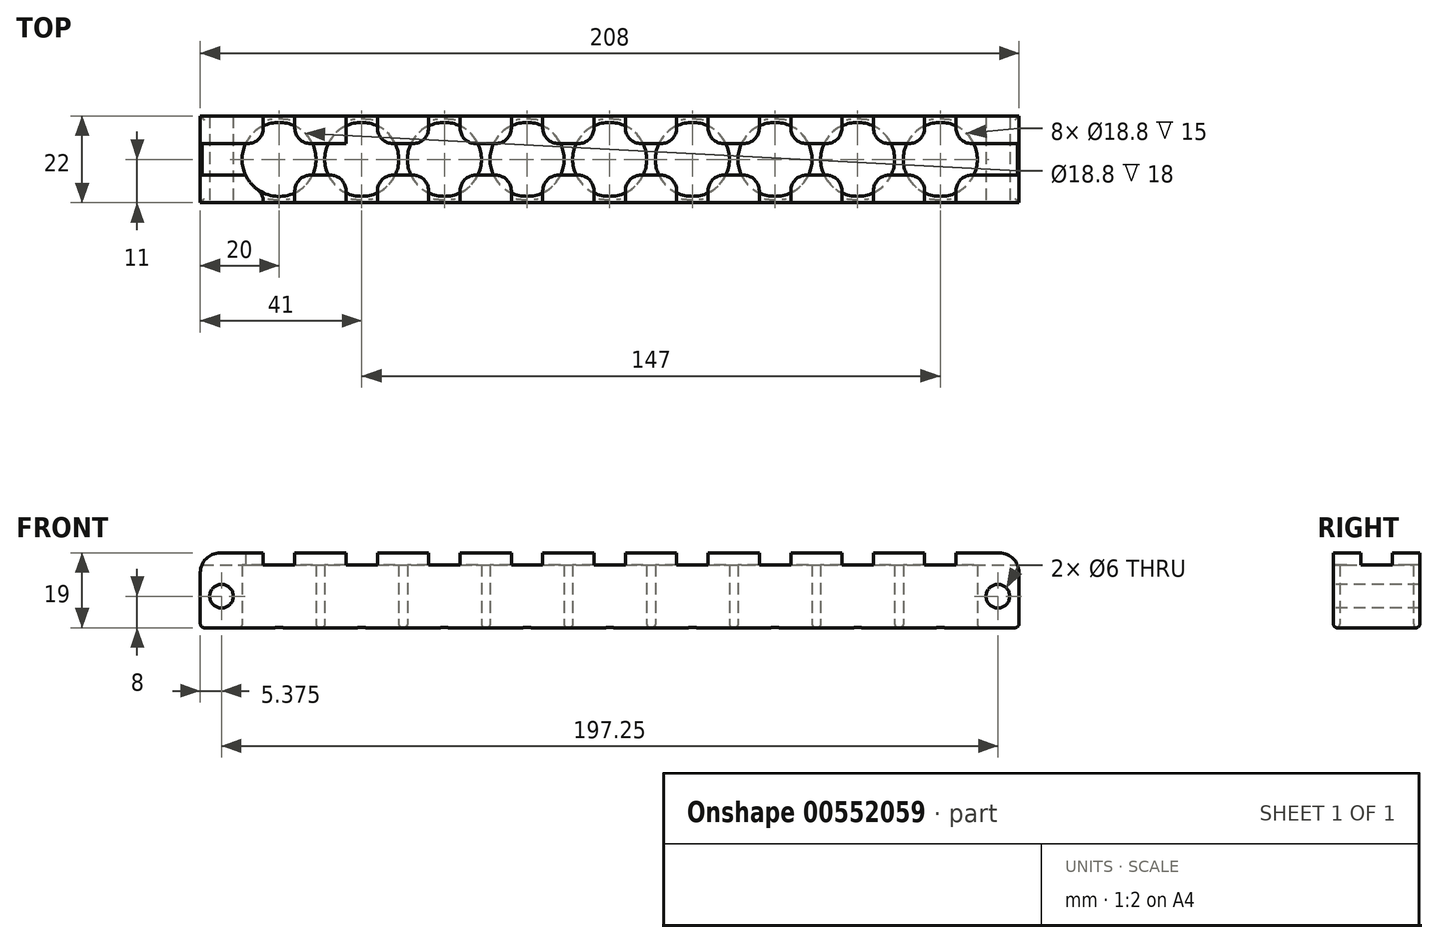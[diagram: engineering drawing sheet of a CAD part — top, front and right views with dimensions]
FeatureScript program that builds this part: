
annotation { "Feature Type Name" : "Feature", "Feature Type Description" : "" }
export const myFeature = defineFeature(function(context is Context, id is Id, definition is map)
    precondition{}
    {
        {
            var Q0;
            Q0=qCreatedBy(makeId("Top.planeOp"),FACE);
            var sketch = newSketch(context, id + "F0", { "sketchPlane" : qUnion([Q0])});
            skCircle(sketch, "E0", {"center": v(0, 0) * mm, "radius": 9.4 * mm});
            skCircle(sketch, "E1", {"center": v(-21, 0) * mm, "radius": 9.4 * mm});
            skCircle(sketch, "E2", {"center": v(-42, 0) * mm, "radius": 9.4 * mm});
            skCircle(sketch, "E3", {"center": v(-63, 0) * mm, "radius": 9.4 * mm});
            skCircle(sketch, "E4", {"center": v(84, 0) * mm, "radius": 9.4 * mm});
            skCircle(sketch, "E5", {"center": v(63, 0) * mm, "radius": 9.4 * mm});
            skCircle(sketch, "E6", {"center": v(42, 0) * mm, "radius": 9.4 * mm});
            skCircle(sketch, "E7", {"center": v(21, 0) * mm, "radius": 9.4 * mm});
            skCircle(sketch, "E8", {"center": v(105, 0) * mm, "radius": 9.4 * mm});
            skLineSegment(sketch, "E9.bottom", {"start": v(-83, 11) * mm, "end": v(125, 11) * mm});
            skLineSegment(sketch, "E9.top", {"start": v(-83, -11) * mm, "end": v(125, -11) * mm});
            skLineSegment(sketch, "E9.left", {"start": v(-83, 11) * mm, "end": v(-83, -11) * mm});
            skLineSegment(sketch, "E9.right", {"start": v(125, 11) * mm, "end": v(125, -11) * mm});
            skSolve(sketch);
        }
        {
            var Q0;
            Q0=makeQuery(id+"F0.imprint","IMPRINT",FACE,{"disambiguationData":[TD([[makeQuery(id+"F0.imprint","IMPRINT",EDGE,{"derivedFrom":sQuery(id+"F0.wireOp",EDGE,"E0")}),-1.0]])]});
            extrude(context, id + "F1", {"entities" : qUnion([Q0]), "depth" : 16 * mm, "offsetDistance" : 25 * mm});
        }
        {
            var Q0;
            Q0=makeQuery(id+"F1.opExtrude","SWEPT_FACE",FACE,{"disambiguationData":[OSD([sQuery(id+"F0.wireOp",EDGE,"E9.top")])]});
            var sketch = newSketch(context, id + "F2", { "sketchPlane" : qUnion([Q0])});
            skCircle(sketch, "E10", {"center": v(119.62, 8) * mm, "radius": 2.6 * mm});
            skPoint(sketch, "E10.centerSnap0", {"position": v(125, 8) * mm});
            skCircle(sketch, "E11", {"center": v(-77.62, 8) * mm, "radius": 2.6 * mm});
            skPoint(sketch, "E12", {"position": v(-83, 8) * mm});
            skSolve(sketch);
        }
        {
            var Q0;
            Q0=makeQuery(id+"F1.opExtrude","CAP_FACE",FACE,{"disambiguationData":[OSD([sQuery(id+"F0.wireOp",EDGE,"E0"),sQuery(id+"F0.wireOp",EDGE,"E1"),sQuery(id+"F0.wireOp",EDGE,"E2"),sQuery(id+"F0.wireOp",EDGE,"E3"),sQuery(id+"F0.wireOp",EDGE,"E4"),sQuery(id+"F0.wireOp",EDGE,"E5"),sQuery(id+"F0.wireOp",EDGE,"E6"),sQuery(id+"F0.wireOp",EDGE,"E7"),sQuery(id+"F0.wireOp",EDGE,"E8"),sQuery(id+"F0.wireOp",EDGE,"E9.bottom"),sQuery(id+"F0.wireOp",EDGE,"E9.top"),sQuery(id+"F0.wireOp",EDGE,"E9.left"),sQuery(id+"F0.wireOp",EDGE,"E9.right")])],"isStart":false});
            var sketch = newSketch(context, id + "F3", { "sketchPlane" : qUnion([Q0])});
            skLineSegment(sketch, "E13", {"start": v(-83, -4) * mm, "end": v(-67, -4) * mm});
            skLineSegment(sketch, "E14", {"start": v(-83, 4) * mm, "end": v(-67, 4) * mm});
            skLineSegment(sketch, "E15", {"start": v(4, 11) * mm, "end": v(4, 4) * mm});
            skLineSegment(sketch, "E16", {"start": v(-4, 11) * mm, "end": v(-4, 4) * mm});
            skLineSegment(sketch, "E17", {"start": v(-59, 11) * mm, "end": v(-59, 4) * mm});
            skLineSegment(sketch, "E18", {"start": v(-67, 11) * mm, "end": v(-67, 4) * mm});
            skLineSegment(sketch, "E19", {"start": v(-38, 11) * mm, "end": v(-38, 4) * mm});
            skLineSegment(sketch, "E20", {"start": v(-46, 11) * mm, "end": v(-46, 4) * mm});
            skLineSegment(sketch, "E21", {"start": v(-46, -11) * mm, "end": v(-38, -11) * mm});
            skLineSegment(sketch, "E22", {"start": v(-25, 11) * mm, "end": v(-25, 4) * mm});
            skLineSegment(sketch, "E23", {"start": v(17, 11) * mm, "end": v(17, 4) * mm});
            skLineSegment(sketch, "E24", {"start": v(17, -11) * mm, "end": v(25, -11) * mm});
            skLineSegment(sketch, "E25", {"start": v(46, 11) * mm, "end": v(46, 4) * mm});
            skLineSegment(sketch, "E26", {"start": v(38, 11) * mm, "end": v(38, 4) * mm});
            skLineSegment(sketch, "E27", {"start": v(38, -11) * mm, "end": v(46, -11) * mm});
            skLineSegment(sketch, "E28", {"start": v(67, 11) * mm, "end": v(67, 4) * mm});
            skLineSegment(sketch, "E29", {"start": v(59, -11) * mm, "end": v(67, -11) * mm});
            skLineSegment(sketch, "E30", {"start": v(88, 11) * mm, "end": v(88, 4) * mm});
            skLineSegment(sketch, "E31", {"start": v(80, 11) * mm, "end": v(80, 4) * mm});
            skLineSegment(sketch, "E32", {"start": v(109, 11) * mm, "end": v(109, 4) * mm});
            skLineSegment(sketch, "E33", {"start": v(101, 11) * mm, "end": v(101, 4) * mm});
            skLineSegment(sketch, "E34", {"start": v(-83, -4) * mm, "end": v(-83, -11) * mm});
            skLineSegment(sketch, "E35", {"start": v(-83, -11) * mm, "end": v(-67, -11) * mm});
            skLineSegment(sketch, "E36", {"start": v(-67, -4) * mm, "end": v(-83, -4) * mm});
            skPoint(sketch, "E37", {"position": v(-67, 4) * mm});
            skPoint(sketch, "E38", {"position": v(-59, 4) * mm});
            skPoint(sketch, "E39", {"position": v(-59, -4) * mm});
            skPoint(sketch, "E40", {"position": v(-46, 4) * mm});
            skPoint(sketch, "E41", {"position": v(-46, -4) * mm});
            skLineSegment(sketch, "E42.trimOffspring", {"start": v(-67, -4) * mm, "end": v(-67, -11) * mm});
            skLineSegment(sketch, "E43.trimOffspring", {"start": v(-59, -4) * mm, "end": v(-46, -4) * mm});
            skLineSegment(sketch, "E44.trimOffspring", {"start": v(-59, -4) * mm, "end": v(-59, -11) * mm});
            skLineSegment(sketch, "E45.trimOffspring", {"start": v(-59, 4) * mm, "end": v(-46, 4) * mm});
            skLineSegment(sketch, "E46.trimOffspring", {"start": v(-46, -4) * mm, "end": v(-46, -11) * mm});
            skLineSegment(sketch, "E47.trimOffspring", {"start": v(-38, 4) * mm, "end": v(-25, 4) * mm});
            skLineSegment(sketch, "E48.trimOffspring", {"start": v(-38, -4) * mm, "end": v(-38, -11) * mm});
            skLineSegment(sketch, "E49.trimOffspring", {"start": v(-25, -4) * mm, "end": v(-25, -11) * mm});
            skLineSegment(sketch, "E50.trimOffspring", {"start": v(-17, 4) * mm, "end": v(-4, 4) * mm});
            skLineSegment(sketch, "E51.trimOffspring", {"start": v(-17, -4) * mm, "end": v(-17, -11) * mm});
            skLineSegment(sketch, "E52", {"start": v(-17, 4) * mm, "end": v(-17, 11) * mm});
            skLineSegment(sketch, "E53.trimOffspring", {"start": v(-4, -4) * mm, "end": v(-4, -11) * mm});
            skLineSegment(sketch, "E54.trimOffspring", {"start": v(4, -4) * mm, "end": v(4, -11) * mm});
            skLineSegment(sketch, "E55.trimOffspring", {"start": v(4, -4) * mm, "end": v(17, -4) * mm});
            skLineSegment(sketch, "E56.trimOffspring", {"start": v(17, -4) * mm, "end": v(17, -11) * mm});
            skLineSegment(sketch, "E57.trimOffspring", {"start": v(25, 4) * mm, "end": v(38, 4) * mm});
            skLineSegment(sketch, "E58.trimOffspring", {"start": v(25, -4) * mm, "end": v(25, -11) * mm});
            skLineSegment(sketch, "E59.trimOffspring", {"start": v(38, -4) * mm, "end": v(38, -11) * mm});
            skLineSegment(sketch, "E60.trimOffspring", {"start": v(46, 4) * mm, "end": v(59, 4) * mm});
            skLineSegment(sketch, "E61.trimOffspring", {"start": v(46, -4) * mm, "end": v(46, -11) * mm});
            skLineSegment(sketch, "E62.trimOffspring", {"start": v(-38, -4) * mm, "end": v(-25, -4) * mm});
            skLineSegment(sketch, "E63.trimOffspring", {"start": v(4, 4) * mm, "end": v(17, 4) * mm});
            skLineSegment(sketch, "E64.trimOffspring", {"start": v(-17, -4) * mm, "end": v(-4, -4) * mm});
            skLineSegment(sketch, "E65.trimOffspring", {"start": v(25, -4) * mm, "end": v(38, -4) * mm});
            skLineSegment(sketch, "E66.trimOffspring", {"start": v(46, -4) * mm, "end": v(59, -4) * mm});
            skLineSegment(sketch, "E67.trimOffspring", {"start": v(67, -4) * mm, "end": v(80, -4) * mm});
            skPoint(sketch, "E68.orphan", {"position": v(25, 11) * mm});
            skLineSegment(sketch, "E69.trimOffspring", {"start": v(67, 4) * mm, "end": v(80, 4) * mm});
            skLineSegment(sketch, "E70.trimOffspring", {"start": v(59, -4) * mm, "end": v(59, -11) * mm});
            skPoint(sketch, "E71.start.orphan", {"position": v(59, 11) * mm});
            skLineSegment(sketch, "E72.trimOffspring", {"start": v(67, -4) * mm, "end": v(67, -11) * mm});
            skLineSegment(sketch, "E73.trimOffspring", {"start": v(80, -4) * mm, "end": v(80, -11) * mm});
            skLineSegment(sketch, "E74.trimOffspring", {"start": v(88, -4) * mm, "end": v(88, -11) * mm});
            skLineSegment(sketch, "E75.trimOffspring", {"start": v(88, 4) * mm, "end": v(101, 4) * mm});
            skPoint(sketch, "E76.orphan", {"position": v(105, 11) * mm});
            skLineSegment(sketch, "E77.trimOffspring", {"start": v(109, 4) * mm, "end": v(125, 4) * mm});
            skLineSegment(sketch, "E78.trimOffspring", {"start": v(109, -4) * mm, "end": v(109, -11) * mm});
            skLineSegment(sketch, "E79.trimOffspring", {"start": v(109, -4) * mm, "end": v(125, -4) * mm});
            skLineSegment(sketch, "E80.trimOffspring", {"start": v(101, -4) * mm, "end": v(101, -11) * mm});
            skLineSegment(sketch, "E81.trimOffspring", {"start": v(88, -4) * mm, "end": v(101, -4) * mm});
            skLineSegment(sketch, "E82", {"start": v(59, 4) * mm, "end": v(59, 11) * mm});
            skLineSegment(sketch, "E83", {"start": v(25, 4) * mm, "end": v(25, 11) * mm});
            skLineSegment(sketch, "E84", {"start": v(-83, 4) * mm, "end": v(-83, 11) * mm});
            skLineSegment(sketch, "E85", {"start": v(-83, 11) * mm, "end": v(-67, 11) * mm});
            skSolve(sketch);
        }
        {
            var Q0;
            {var subQ0=sQuery(id+"F3.wireOp",EDGE,"E84");Q0=makeQuery(id+"F3.imprint","IMPRINT",FACE,{"disambiguationData":[TD([[makeQuery(id+"F3.imprint","IMPRINT",EDGE,{"derivedFrom":subQ0}),1.0]])]});}
            var Q1;
            {var subQ0=sQuery(id+"F3.wireOp",EDGE,"E18");var subQ1=sQuery(id+"F3.wireOp",EDGE,"E14");var subQ2=makeQuery(id+"F3.imprint","INTERSECT",VERTEX,{"derivedFrom":[subQ1,subQ0]});Q1=makeQuery(id+"F3.imprint","IMPRINT",FACE,{"disambiguationData":[TD([[makeQuery(id+"F3.imprint","IMPRINT",EDGE,{"disambiguationData":[TD([[subQ2,1.0]])],"derivedFrom":subQ1}),1.0]])]});}
            var Q2;
            {var subQ1=sQuery(id+"F3.wireOp",EDGE,"E34");Q2=makeQuery(id+"F3.imprint","IMPRINT",FACE,{"disambiguationData":[TD([[makeQuery(id+"F3.imprint","IMPRINT",EDGE,{"derivedFrom":subQ1}),1.0]])]});}
            var Q3;
            {var subQ0=sQuery(id+"F3.wireOp",EDGE,"E42.trimOffspring");var subQ1=sQuery(id+"F3.wireOp",EDGE,"E36");var subQ2=makeQuery(id+"F3.imprint","INTERSECT",VERTEX,{"derivedFrom":[subQ1,subQ0]});Q3=makeQuery(id+"F3.imprint","IMPRINT",FACE,{"disambiguationData":[TD([[makeQuery(id+"F3.imprint","IMPRINT",EDGE,{"disambiguationData":[TD([[subQ2,-1.0]])],"derivedFrom":subQ1}),1.0]])]});}
            var Q4;
            {var subQ0=sQuery(id+"F3.wireOp",EDGE,"E45.trimOffspring");var subQ1=sQuery(id+"F3.wireOp",EDGE,"E17");var subQ2=makeQuery(id+"F3.imprint","INTERSECT",VERTEX,{"derivedFrom":[subQ1,subQ0]});Q4=makeQuery(id+"F3.imprint","IMPRINT",FACE,{"disambiguationData":[TD([[makeQuery(id+"F3.imprint","IMPRINT",EDGE,{"disambiguationData":[TD([[subQ2,1.0]])],"derivedFrom":subQ1}),1.0]])]});}
            var Q5;
            {var subQ5=sQuery(id+"F3.wireOp",EDGE,"E17");var subQ6=makeQuery(id+"F1.opExtrude","CAP_EDGE",EDGE,{"disambiguationData":[OSD([sQuery(id+"F0.wireOp",EDGE,"E9.bottom")])],"isStart":false});var subQ7=makeQuery(id+"F3.imprint","INTERSECT",VERTEX,{"derivedFrom":[subQ6,subQ5]});Q5=makeQuery(id+"F3.imprint","IMPRINT",FACE,{"disambiguationData":[TD([[makeQuery(id+"F3.imprint","IMPRINT",EDGE,{"disambiguationData":[TD([[subQ7,-1.0]])],"derivedFrom":subQ5}),1.0]])]});}
            var Q6;
            {var subQ0=sQuery(id+"F3.wireOp",EDGE,"E45.trimOffspring");var subQ1=sQuery(id+"F3.wireOp",EDGE,"E20");var subQ2=makeQuery(id+"F3.imprint","INTERSECT",VERTEX,{"derivedFrom":[subQ1,subQ0]});Q6=makeQuery(id+"F3.imprint","IMPRINT",FACE,{"disambiguationData":[TD([[makeQuery(id+"F3.imprint","IMPRINT",EDGE,{"disambiguationData":[TD([[subQ2,1.0]])],"derivedFrom":subQ1}),-1.0]])]});}
            var Q7;
            {var subQ0=sQuery(id+"F3.wireOp",EDGE,"E44.trimOffspring");var subQ1=sQuery(id+"F3.wireOp",EDGE,"E43.trimOffspring");var subQ2=makeQuery(id+"F3.imprint","INTERSECT",VERTEX,{"derivedFrom":[subQ1,subQ0]});Q7=makeQuery(id+"F3.imprint","IMPRINT",FACE,{"disambiguationData":[TD([[makeQuery(id+"F3.imprint","IMPRINT",EDGE,{"disambiguationData":[TD([[subQ2,-1.0]])],"derivedFrom":subQ1}),-1.0]])]});}
            var Q8;
            {var subQ0=sQuery(id+"F3.wireOp",EDGE,"E46.trimOffspring");var subQ1=sQuery(id+"F3.wireOp",EDGE,"E43.trimOffspring");var subQ2=makeQuery(id+"F3.imprint","INTERSECT",VERTEX,{"derivedFrom":[subQ1,subQ0]});Q8=makeQuery(id+"F3.imprint","IMPRINT",FACE,{"disambiguationData":[TD([[makeQuery(id+"F3.imprint","IMPRINT",EDGE,{"disambiguationData":[TD([[subQ2,1.0]])],"derivedFrom":subQ1}),-1.0]])]});}
            var Q9;
            {var subQ5=makeQuery(id+"F1.opExtrude","CAP_EDGE",EDGE,{"disambiguationData":[OSD([sQuery(id+"F0.wireOp",EDGE,"E3")])],"isStart":false});var subQ9=sQuery(id+"F3.wireOp",EDGE,"E43.trimOffspring");var subQ10=makeQuery(id+"F3.imprint","INTERSECT",VERTEX,{"derivedFrom":[subQ5,subQ9]});Q9=makeQuery(id+"F3.imprint","IMPRINT",FACE,{"disambiguationData":[TD([[makeQuery(id+"F3.imprint","IMPRINT",EDGE,{"disambiguationData":[TD([[subQ10,-1.0]])],"derivedFrom":subQ9}),-1.0]])]});}
            var Q10;
            {var subQ1=makeQuery(id+"F1.opExtrude","CAP_EDGE",EDGE,{"disambiguationData":[OSD([sQuery(id+"F0.wireOp",EDGE,"E9.top")])],"isStart":false});var subQ3=sQuery(id+"F3.wireOp",EDGE,"E49.trimOffspring");var subQ4=makeQuery(id+"F3.imprint","INTERSECT",VERTEX,{"derivedFrom":[subQ1,subQ3]});Q10=makeQuery(id+"F3.imprint","IMPRINT",FACE,{"disambiguationData":[TD([[makeQuery(id+"F3.imprint","IMPRINT",EDGE,{"disambiguationData":[TD([[subQ4,1.0]])],"derivedFrom":subQ3}),-1.0]])]});}
            var Q11;
            {var subQ0=sQuery(id+"F3.wireOp",EDGE,"E62.trimOffspring");var subQ1=sQuery(id+"F3.wireOp",EDGE,"E48.trimOffspring");var subQ2=makeQuery(id+"F3.imprint","INTERSECT",VERTEX,{"derivedFrom":[subQ1,subQ0]});Q11=makeQuery(id+"F3.imprint","IMPRINT",FACE,{"disambiguationData":[TD([[makeQuery(id+"F3.imprint","IMPRINT",EDGE,{"disambiguationData":[TD([[subQ2,-1.0]])],"derivedFrom":subQ1}),1.0]])]});}
            var Q12;
            {var subQ0=sQuery(id+"F3.wireOp",EDGE,"E62.trimOffspring");var subQ1=sQuery(id+"F3.wireOp",EDGE,"E49.trimOffspring");var subQ2=makeQuery(id+"F3.imprint","INTERSECT",VERTEX,{"derivedFrom":[subQ1,subQ0]});Q12=makeQuery(id+"F3.imprint","IMPRINT",FACE,{"disambiguationData":[TD([[makeQuery(id+"F3.imprint","IMPRINT",EDGE,{"disambiguationData":[TD([[subQ2,-1.0]])],"derivedFrom":subQ1}),-1.0]])]});}
            var Q13;
            {var subQ0=sQuery(id+"F3.wireOp",EDGE,"E19");var subQ1=makeQuery(id+"F1.opExtrude","CAP_EDGE",EDGE,{"disambiguationData":[OSD([sQuery(id+"F0.wireOp",EDGE,"E9.bottom")])],"isStart":false});var subQ2=makeQuery(id+"F3.imprint","INTERSECT",VERTEX,{"derivedFrom":[subQ1,subQ0]});Q13=makeQuery(id+"F3.imprint","IMPRINT",FACE,{"disambiguationData":[TD([[makeQuery(id+"F3.imprint","IMPRINT",EDGE,{"disambiguationData":[TD([[subQ2,-1.0]])],"derivedFrom":subQ0}),1.0]])]});}
            var Q14;
            {var subQ0=sQuery(id+"F3.wireOp",EDGE,"E47.trimOffspring");var subQ1=sQuery(id+"F3.wireOp",EDGE,"E22");var subQ2=makeQuery(id+"F3.imprint","INTERSECT",VERTEX,{"derivedFrom":[subQ1,subQ0]});Q14=makeQuery(id+"F3.imprint","IMPRINT",FACE,{"disambiguationData":[TD([[makeQuery(id+"F3.imprint","IMPRINT",EDGE,{"disambiguationData":[TD([[subQ2,1.0]])],"derivedFrom":subQ1}),-1.0]])]});}
            var Q15;
            {var subQ0=sQuery(id+"F3.wireOp",EDGE,"E47.trimOffspring");var subQ1=sQuery(id+"F3.wireOp",EDGE,"E19");var subQ2=makeQuery(id+"F3.imprint","INTERSECT",VERTEX,{"derivedFrom":[subQ1,subQ0]});Q15=makeQuery(id+"F3.imprint","IMPRINT",FACE,{"disambiguationData":[TD([[makeQuery(id+"F3.imprint","IMPRINT",EDGE,{"disambiguationData":[TD([[subQ2,1.0]])],"derivedFrom":subQ1}),1.0]])]});}
            var Q16;
            {var subQ0=sQuery(id+"F3.wireOp",EDGE,"E52");var subQ1=sQuery(id+"F3.wireOp",EDGE,"E50.trimOffspring");var subQ2=makeQuery(id+"F3.imprint","INTERSECT",VERTEX,{"derivedFrom":[subQ1,subQ0]});Q16=makeQuery(id+"F3.imprint","IMPRINT",FACE,{"disambiguationData":[TD([[makeQuery(id+"F3.imprint","IMPRINT",EDGE,{"disambiguationData":[TD([[subQ2,-1.0]])],"derivedFrom":subQ1}),1.0]])]});}
            var Q17;
            {var subQ0=sQuery(id+"F3.wireOp",EDGE,"E16");var subQ1=makeQuery(id+"F1.opExtrude","CAP_EDGE",EDGE,{"disambiguationData":[OSD([sQuery(id+"F0.wireOp",EDGE,"E9.bottom")])],"isStart":false});var subQ2=makeQuery(id+"F3.imprint","INTERSECT",VERTEX,{"derivedFrom":[subQ1,subQ0]});Q17=makeQuery(id+"F3.imprint","IMPRINT",FACE,{"disambiguationData":[TD([[makeQuery(id+"F3.imprint","IMPRINT",EDGE,{"disambiguationData":[TD([[subQ2,-1.0]])],"derivedFrom":subQ0}),-1.0]])]});}
            var Q18;
            {var subQ0=sQuery(id+"F3.wireOp",EDGE,"E50.trimOffspring");var subQ1=sQuery(id+"F3.wireOp",EDGE,"E16");var subQ2=makeQuery(id+"F3.imprint","INTERSECT",VERTEX,{"derivedFrom":[subQ1,subQ0]});Q18=makeQuery(id+"F3.imprint","IMPRINT",FACE,{"disambiguationData":[TD([[makeQuery(id+"F3.imprint","IMPRINT",EDGE,{"disambiguationData":[TD([[subQ2,1.0]])],"derivedFrom":subQ1}),-1.0]])]});}
            var Q19;
            {var subQ0=sQuery(id+"F3.wireOp",EDGE,"E51.trimOffspring");var subQ1=makeQuery(id+"F1.opExtrude","CAP_EDGE",EDGE,{"disambiguationData":[OSD([sQuery(id+"F0.wireOp",EDGE,"E9.top")])],"isStart":false});var subQ2=makeQuery(id+"F3.imprint","INTERSECT",VERTEX,{"derivedFrom":[subQ1,subQ0]});Q19=makeQuery(id+"F3.imprint","IMPRINT",FACE,{"disambiguationData":[TD([[makeQuery(id+"F3.imprint","IMPRINT",EDGE,{"disambiguationData":[TD([[subQ2,1.0]])],"derivedFrom":subQ0}),1.0]])]});}
            var Q20;
            {var subQ0=sQuery(id+"F3.wireOp",EDGE,"E64.trimOffspring");var subQ1=sQuery(id+"F3.wireOp",EDGE,"E51.trimOffspring");var subQ2=makeQuery(id+"F3.imprint","INTERSECT",VERTEX,{"derivedFrom":[subQ1,subQ0]});Q20=makeQuery(id+"F3.imprint","IMPRINT",FACE,{"disambiguationData":[TD([[makeQuery(id+"F3.imprint","IMPRINT",EDGE,{"disambiguationData":[TD([[subQ2,-1.0]])],"derivedFrom":subQ1}),1.0]])]});}
            var Q21;
            {var subQ0=sQuery(id+"F3.wireOp",EDGE,"E64.trimOffspring");var subQ1=sQuery(id+"F3.wireOp",EDGE,"E53.trimOffspring");var subQ2=makeQuery(id+"F3.imprint","INTERSECT",VERTEX,{"derivedFrom":[subQ1,subQ0]});Q21=makeQuery(id+"F3.imprint","IMPRINT",FACE,{"disambiguationData":[TD([[makeQuery(id+"F3.imprint","IMPRINT",EDGE,{"disambiguationData":[TD([[subQ2,-1.0]])],"derivedFrom":subQ1}),-1.0]])]});}
            var Q22;
            {var subQ0=sQuery(id+"F3.wireOp",EDGE,"E63.trimOffspring");var subQ1=sQuery(id+"F3.wireOp",EDGE,"E15");var subQ2=makeQuery(id+"F3.imprint","INTERSECT",VERTEX,{"derivedFrom":[subQ1,subQ0]});Q22=makeQuery(id+"F3.imprint","IMPRINT",FACE,{"disambiguationData":[TD([[makeQuery(id+"F3.imprint","IMPRINT",EDGE,{"disambiguationData":[TD([[subQ2,1.0]])],"derivedFrom":subQ1}),1.0]])]});}
            var Q23;
            {var subQ0=sQuery(id+"F3.wireOp",EDGE,"E15");var subQ1=makeQuery(id+"F1.opExtrude","CAP_EDGE",EDGE,{"disambiguationData":[OSD([sQuery(id+"F0.wireOp",EDGE,"E9.bottom")])],"isStart":false});var subQ2=makeQuery(id+"F3.imprint","INTERSECT",VERTEX,{"derivedFrom":[subQ1,subQ0]});Q23=makeQuery(id+"F3.imprint","IMPRINT",FACE,{"disambiguationData":[TD([[makeQuery(id+"F3.imprint","IMPRINT",EDGE,{"disambiguationData":[TD([[subQ2,-1.0]])],"derivedFrom":subQ0}),1.0]])]});}
            var Q24;
            {var subQ0=sQuery(id+"F3.wireOp",EDGE,"E63.trimOffspring");var subQ1=sQuery(id+"F3.wireOp",EDGE,"E23");var subQ2=makeQuery(id+"F3.imprint","INTERSECT",VERTEX,{"derivedFrom":[subQ1,subQ0]});Q24=makeQuery(id+"F3.imprint","IMPRINT",FACE,{"disambiguationData":[TD([[makeQuery(id+"F3.imprint","IMPRINT",EDGE,{"disambiguationData":[TD([[subQ2,1.0]])],"derivedFrom":subQ1}),-1.0]])]});}
            var Q25;
            {var subQ0=sQuery(id+"F3.wireOp",EDGE,"E55.trimOffspring");var subQ1=sQuery(id+"F3.wireOp",EDGE,"E54.trimOffspring");var subQ2=makeQuery(id+"F3.imprint","INTERSECT",VERTEX,{"derivedFrom":[subQ1,subQ0]});Q25=makeQuery(id+"F3.imprint","IMPRINT",FACE,{"disambiguationData":[TD([[makeQuery(id+"F3.imprint","IMPRINT",EDGE,{"disambiguationData":[TD([[subQ2,-1.0]])],"derivedFrom":subQ1}),1.0]])]});}
            var Q26;
            {var subQ1=makeQuery(id+"F1.opExtrude","CAP_EDGE",EDGE,{"disambiguationData":[OSD([sQuery(id+"F0.wireOp",EDGE,"E9.top")])],"isStart":false});var subQ3=sQuery(id+"F3.wireOp",EDGE,"E54.trimOffspring");var subQ4=makeQuery(id+"F3.imprint","INTERSECT",VERTEX,{"derivedFrom":[subQ1,subQ3]});Q26=makeQuery(id+"F3.imprint","IMPRINT",FACE,{"disambiguationData":[TD([[makeQuery(id+"F3.imprint","IMPRINT",EDGE,{"disambiguationData":[TD([[subQ4,1.0]])],"derivedFrom":subQ3}),1.0]])]});}
            var Q27;
            {var subQ0=sQuery(id+"F3.wireOp",EDGE,"E56.trimOffspring");var subQ1=sQuery(id+"F3.wireOp",EDGE,"E55.trimOffspring");var subQ2=makeQuery(id+"F3.imprint","INTERSECT",VERTEX,{"derivedFrom":[subQ1,subQ0]});Q27=makeQuery(id+"F3.imprint","IMPRINT",FACE,{"disambiguationData":[TD([[makeQuery(id+"F3.imprint","IMPRINT",EDGE,{"disambiguationData":[TD([[subQ2,1.0]])],"derivedFrom":subQ1}),-1.0]])]});}
            var Q28;
            {var subQ0=sQuery(id+"F3.wireOp",EDGE,"E65.trimOffspring");var subQ1=sQuery(id+"F3.wireOp",EDGE,"E58.trimOffspring");var subQ2=makeQuery(id+"F3.imprint","INTERSECT",VERTEX,{"derivedFrom":[subQ1,subQ0]});Q28=makeQuery(id+"F3.imprint","IMPRINT",FACE,{"disambiguationData":[TD([[makeQuery(id+"F3.imprint","IMPRINT",EDGE,{"disambiguationData":[TD([[subQ2,-1.0]])],"derivedFrom":subQ1}),1.0]])]});}
            var Q29;
            {var subQ0=sQuery(id+"F3.wireOp",EDGE,"E65.trimOffspring");var subQ1=makeQuery(id+"F1.opExtrude","CAP_EDGE",EDGE,{"disambiguationData":[OSD([sQuery(id+"F0.wireOp",EDGE,"E7")])],"isStart":false});var subQ2=makeQuery(id+"F3.imprint","INTERSECT",VERTEX,{"derivedFrom":[subQ1,subQ0]});Q29=makeQuery(id+"F3.imprint","IMPRINT",FACE,{"disambiguationData":[TD([[makeQuery(id+"F3.imprint","IMPRINT",EDGE,{"disambiguationData":[TD([[subQ2,-1.0]])],"derivedFrom":subQ0}),-1.0]])]});}
            var Q30;
            {var subQ0=sQuery(id+"F3.wireOp",EDGE,"E65.trimOffspring");var subQ1=sQuery(id+"F3.wireOp",EDGE,"E59.trimOffspring");var subQ2=makeQuery(id+"F3.imprint","INTERSECT",VERTEX,{"derivedFrom":[subQ1,subQ0]});Q30=makeQuery(id+"F3.imprint","IMPRINT",FACE,{"disambiguationData":[TD([[makeQuery(id+"F3.imprint","IMPRINT",EDGE,{"disambiguationData":[TD([[subQ2,-1.0]])],"derivedFrom":subQ1}),-1.0]])]});}
            var Q31;
            {var subQ0=sQuery(id+"F3.wireOp",EDGE,"E83");var subQ1=sQuery(id+"F3.wireOp",EDGE,"E57.trimOffspring");var subQ2=makeQuery(id+"F3.imprint","INTERSECT",VERTEX,{"derivedFrom":[subQ1,subQ0]});Q31=makeQuery(id+"F3.imprint","IMPRINT",FACE,{"disambiguationData":[TD([[makeQuery(id+"F3.imprint","IMPRINT",EDGE,{"disambiguationData":[TD([[subQ2,-1.0]])],"derivedFrom":subQ1}),1.0]])]});}
            var Q32;
            {var subQ0=sQuery(id+"F3.wireOp",EDGE,"E57.trimOffspring");var subQ1=sQuery(id+"F3.wireOp",EDGE,"E26");var subQ2=makeQuery(id+"F3.imprint","INTERSECT",VERTEX,{"derivedFrom":[subQ1,subQ0]});Q32=makeQuery(id+"F3.imprint","IMPRINT",FACE,{"disambiguationData":[TD([[makeQuery(id+"F3.imprint","IMPRINT",EDGE,{"disambiguationData":[TD([[subQ2,1.0]])],"derivedFrom":subQ1}),-1.0]])]});}
            var Q33;
            {var subQ1=makeQuery(id+"F1.opExtrude","CAP_EDGE",EDGE,{"disambiguationData":[OSD([sQuery(id+"F0.wireOp",EDGE,"E9.bottom")])],"isStart":false});var subQ5=sQuery(id+"F3.wireOp",EDGE,"E25");var subQ6=makeQuery(id+"F3.imprint","INTERSECT",VERTEX,{"derivedFrom":[subQ1,subQ5]});Q33=makeQuery(id+"F3.imprint","IMPRINT",FACE,{"disambiguationData":[TD([[makeQuery(id+"F3.imprint","IMPRINT",EDGE,{"disambiguationData":[TD([[subQ6,-1.0]])],"derivedFrom":subQ5}),1.0]])]});}
            var Q34;
            {var subQ0=sQuery(id+"F3.wireOp",EDGE,"E60.trimOffspring");var subQ1=sQuery(id+"F3.wireOp",EDGE,"E25");var subQ2=makeQuery(id+"F3.imprint","INTERSECT",VERTEX,{"derivedFrom":[subQ1,subQ0]});Q34=makeQuery(id+"F3.imprint","IMPRINT",FACE,{"disambiguationData":[TD([[makeQuery(id+"F3.imprint","IMPRINT",EDGE,{"disambiguationData":[TD([[subQ2,1.0]])],"derivedFrom":subQ1}),1.0]])]});}
            var Q35;
            {var subQ0=sQuery(id+"F3.wireOp",EDGE,"E82");var subQ1=sQuery(id+"F3.wireOp",EDGE,"E60.trimOffspring");var subQ2=makeQuery(id+"F3.imprint","INTERSECT",VERTEX,{"derivedFrom":[subQ1,subQ0]});Q35=makeQuery(id+"F3.imprint","IMPRINT",FACE,{"disambiguationData":[TD([[makeQuery(id+"F3.imprint","IMPRINT",EDGE,{"disambiguationData":[TD([[subQ2,1.0]])],"derivedFrom":subQ1}),1.0]])]});}
            var Q36;
            {var subQ7=sQuery(id+"F3.wireOp",EDGE,"E66.trimOffspring");var subQ8=makeQuery(id+"F1.opExtrude","CAP_EDGE",EDGE,{"disambiguationData":[OSD([sQuery(id+"F0.wireOp",EDGE,"E6")])],"isStart":false});var subQ9=makeQuery(id+"F3.imprint","INTERSECT",VERTEX,{"derivedFrom":[subQ8,subQ7]});Q36=makeQuery(id+"F3.imprint","IMPRINT",FACE,{"disambiguationData":[TD([[makeQuery(id+"F3.imprint","IMPRINT",EDGE,{"disambiguationData":[TD([[subQ9,-1.0]])],"derivedFrom":subQ7}),-1.0]])]});}
            var Q37;
            {var subQ0=sQuery(id+"F3.wireOp",EDGE,"E66.trimOffspring");var subQ1=sQuery(id+"F3.wireOp",EDGE,"E61.trimOffspring");var subQ2=makeQuery(id+"F3.imprint","INTERSECT",VERTEX,{"derivedFrom":[subQ1,subQ0]});Q37=makeQuery(id+"F3.imprint","IMPRINT",FACE,{"disambiguationData":[TD([[makeQuery(id+"F3.imprint","IMPRINT",EDGE,{"disambiguationData":[TD([[subQ2,-1.0]])],"derivedFrom":subQ1}),1.0]])]});}
            var Q38;
            {var subQ0=sQuery(id+"F3.wireOp",EDGE,"E26");var subQ1=makeQuery(id+"F1.opExtrude","CAP_EDGE",EDGE,{"disambiguationData":[OSD([sQuery(id+"F0.wireOp",EDGE,"E9.bottom")])],"isStart":false});var subQ2=makeQuery(id+"F3.imprint","INTERSECT",VERTEX,{"derivedFrom":[subQ1,subQ0]});Q38=makeQuery(id+"F3.imprint","IMPRINT",FACE,{"disambiguationData":[TD([[makeQuery(id+"F3.imprint","IMPRINT",EDGE,{"disambiguationData":[TD([[subQ2,-1.0]])],"derivedFrom":subQ0}),-1.0]])]});}
            var Q39;
            {var subQ0=sQuery(id+"F3.wireOp",EDGE,"E70.trimOffspring");var subQ1=sQuery(id+"F3.wireOp",EDGE,"E66.trimOffspring");var subQ2=makeQuery(id+"F3.imprint","INTERSECT",VERTEX,{"derivedFrom":[subQ1,subQ0]});Q39=makeQuery(id+"F3.imprint","IMPRINT",FACE,{"disambiguationData":[TD([[makeQuery(id+"F3.imprint","IMPRINT",EDGE,{"disambiguationData":[TD([[subQ2,1.0]])],"derivedFrom":subQ1}),-1.0]])]});}
            var Q40;
            {var subQ5=makeQuery(id+"F1.opExtrude","CAP_EDGE",EDGE,{"disambiguationData":[OSD([sQuery(id+"F0.wireOp",EDGE,"E5")])],"isStart":false});var subQ9=sQuery(id+"F3.wireOp",EDGE,"E67.trimOffspring");var subQ10=makeQuery(id+"F3.imprint","INTERSECT",VERTEX,{"derivedFrom":[subQ5,subQ9]});Q40=makeQuery(id+"F3.imprint","IMPRINT",FACE,{"disambiguationData":[TD([[makeQuery(id+"F3.imprint","IMPRINT",EDGE,{"disambiguationData":[TD([[subQ10,-1.0]])],"derivedFrom":subQ9}),-1.0]])]});}
            var Q41;
            {var subQ5=sQuery(id+"F3.wireOp",EDGE,"E28");var subQ6=makeQuery(id+"F1.opExtrude","CAP_EDGE",EDGE,{"disambiguationData":[OSD([sQuery(id+"F0.wireOp",EDGE,"E9.bottom")])],"isStart":false});var subQ7=makeQuery(id+"F3.imprint","INTERSECT",VERTEX,{"derivedFrom":[subQ6,subQ5]});Q41=makeQuery(id+"F3.imprint","IMPRINT",FACE,{"disambiguationData":[TD([[makeQuery(id+"F3.imprint","IMPRINT",EDGE,{"disambiguationData":[TD([[subQ7,-1.0]])],"derivedFrom":subQ5}),1.0]])]});}
            var Q42;
            {var subQ0=sQuery(id+"F3.wireOp",EDGE,"E69.trimOffspring");var subQ1=sQuery(id+"F3.wireOp",EDGE,"E28");var subQ2=makeQuery(id+"F3.imprint","INTERSECT",VERTEX,{"derivedFrom":[subQ1,subQ0]});Q42=makeQuery(id+"F3.imprint","IMPRINT",FACE,{"disambiguationData":[TD([[makeQuery(id+"F3.imprint","IMPRINT",EDGE,{"disambiguationData":[TD([[subQ2,1.0]])],"derivedFrom":subQ1}),1.0]])]});}
            var Q43;
            {var subQ0=sQuery(id+"F3.wireOp",EDGE,"E72.trimOffspring");var subQ1=sQuery(id+"F3.wireOp",EDGE,"E67.trimOffspring");var subQ2=makeQuery(id+"F3.imprint","INTERSECT",VERTEX,{"derivedFrom":[subQ1,subQ0]});Q43=makeQuery(id+"F3.imprint","IMPRINT",FACE,{"disambiguationData":[TD([[makeQuery(id+"F3.imprint","IMPRINT",EDGE,{"disambiguationData":[TD([[subQ2,-1.0]])],"derivedFrom":subQ1}),-1.0]])]});}
            var Q44;
            {var subQ0=sQuery(id+"F3.wireOp",EDGE,"E69.trimOffspring");var subQ1=sQuery(id+"F3.wireOp",EDGE,"E31");var subQ2=makeQuery(id+"F3.imprint","INTERSECT",VERTEX,{"derivedFrom":[subQ1,subQ0]});Q44=makeQuery(id+"F3.imprint","IMPRINT",FACE,{"disambiguationData":[TD([[makeQuery(id+"F3.imprint","IMPRINT",EDGE,{"disambiguationData":[TD([[subQ2,1.0]])],"derivedFrom":subQ1}),-1.0]])]});}
            var Q45;
            {var subQ0=sQuery(id+"F3.wireOp",EDGE,"E73.trimOffspring");var subQ1=sQuery(id+"F3.wireOp",EDGE,"E67.trimOffspring");var subQ2=makeQuery(id+"F3.imprint","INTERSECT",VERTEX,{"derivedFrom":[subQ1,subQ0]});Q45=makeQuery(id+"F3.imprint","IMPRINT",FACE,{"disambiguationData":[TD([[makeQuery(id+"F3.imprint","IMPRINT",EDGE,{"disambiguationData":[TD([[subQ2,1.0]])],"derivedFrom":subQ1}),-1.0]])]});}
            var Q46;
            {var subQ5=sQuery(id+"F3.wireOp",EDGE,"E30");var subQ9=makeQuery(id+"F1.opExtrude","CAP_EDGE",EDGE,{"disambiguationData":[OSD([sQuery(id+"F0.wireOp",EDGE,"E9.bottom")])],"isStart":false});var subQ11=makeQuery(id+"F3.imprint","INTERSECT",VERTEX,{"derivedFrom":[subQ9,subQ5]});Q46=makeQuery(id+"F3.imprint","IMPRINT",FACE,{"disambiguationData":[TD([[makeQuery(id+"F3.imprint","IMPRINT",EDGE,{"disambiguationData":[TD([[subQ11,-1.0]])],"derivedFrom":subQ5}),1.0]])]});}
            var Q47;
            {var subQ0=sQuery(id+"F3.wireOp",EDGE,"E75.trimOffspring");var subQ1=sQuery(id+"F3.wireOp",EDGE,"E30");var subQ2=makeQuery(id+"F3.imprint","INTERSECT",VERTEX,{"derivedFrom":[subQ1,subQ0]});Q47=makeQuery(id+"F3.imprint","IMPRINT",FACE,{"disambiguationData":[TD([[makeQuery(id+"F3.imprint","IMPRINT",EDGE,{"disambiguationData":[TD([[subQ2,1.0]])],"derivedFrom":subQ1}),1.0]])]});}
            var Q48;
            {var subQ0=sQuery(id+"F3.wireOp",EDGE,"E75.trimOffspring");var subQ1=sQuery(id+"F3.wireOp",EDGE,"E33");var subQ2=makeQuery(id+"F3.imprint","INTERSECT",VERTEX,{"derivedFrom":[subQ1,subQ0]});Q48=makeQuery(id+"F3.imprint","IMPRINT",FACE,{"disambiguationData":[TD([[makeQuery(id+"F3.imprint","IMPRINT",EDGE,{"disambiguationData":[TD([[subQ2,1.0]])],"derivedFrom":subQ1}),-1.0]])]});}
            var Q49;
            {var subQ0=sQuery(id+"F3.wireOp",EDGE,"E74.trimOffspring");var subQ1=makeQuery(id+"F1.opExtrude","CAP_EDGE",EDGE,{"disambiguationData":[OSD([sQuery(id+"F0.wireOp",EDGE,"E9.top")])],"isStart":false});var subQ2=makeQuery(id+"F3.imprint","INTERSECT",VERTEX,{"derivedFrom":[subQ1,subQ0]});Q49=makeQuery(id+"F3.imprint","IMPRINT",FACE,{"disambiguationData":[TD([[makeQuery(id+"F3.imprint","IMPRINT",EDGE,{"disambiguationData":[TD([[subQ2,1.0]])],"derivedFrom":subQ0}),1.0]])]});}
            var Q50;
            {var subQ1=makeQuery(id+"F1.opExtrude","CAP_EDGE",EDGE,{"disambiguationData":[OSD([sQuery(id+"F0.wireOp",EDGE,"E9.top")])],"isStart":false});var subQ5=sQuery(id+"F3.wireOp",EDGE,"E78.trimOffspring");var subQ6=makeQuery(id+"F3.imprint","INTERSECT",VERTEX,{"derivedFrom":[subQ1,subQ5]});Q50=makeQuery(id+"F3.imprint","IMPRINT",FACE,{"disambiguationData":[TD([[makeQuery(id+"F3.imprint","IMPRINT",EDGE,{"disambiguationData":[TD([[subQ6,1.0]])],"derivedFrom":subQ5}),1.0]])]});}
            var Q51;
            {var subQ1=makeQuery(id+"F1.opExtrude","CAP_EDGE",EDGE,{"disambiguationData":[OSD([sQuery(id+"F0.wireOp",EDGE,"E9.bottom")])],"isStart":false});var subQ7=sQuery(id+"F3.wireOp",EDGE,"E32");var subQ8=makeQuery(id+"F3.imprint","INTERSECT",VERTEX,{"derivedFrom":[subQ1,subQ7]});Q51=makeQuery(id+"F3.imprint","IMPRINT",FACE,{"disambiguationData":[TD([[makeQuery(id+"F3.imprint","IMPRINT",EDGE,{"disambiguationData":[TD([[subQ8,-1.0]])],"derivedFrom":subQ7}),1.0]])]});}
            var Q52;
            {var subQ0=sQuery(id+"F3.wireOp",EDGE,"E77.trimOffspring");var subQ1=sQuery(id+"F3.wireOp",EDGE,"E32");var subQ2=makeQuery(id+"F3.imprint","INTERSECT",VERTEX,{"derivedFrom":[subQ1,subQ0]});Q52=makeQuery(id+"F3.imprint","IMPRINT",FACE,{"disambiguationData":[TD([[makeQuery(id+"F3.imprint","IMPRINT",EDGE,{"disambiguationData":[TD([[subQ2,1.0]])],"derivedFrom":subQ1}),1.0]])]});}
            var Q53;
            {var subQ0=sQuery(id+"F3.wireOp",EDGE,"E79.trimOffspring");var subQ1=sQuery(id+"F3.wireOp",EDGE,"E78.trimOffspring");var subQ2=makeQuery(id+"F3.imprint","INTERSECT",VERTEX,{"derivedFrom":[subQ1,subQ0]});Q53=makeQuery(id+"F3.imprint","IMPRINT",FACE,{"disambiguationData":[TD([[makeQuery(id+"F3.imprint","IMPRINT",EDGE,{"disambiguationData":[TD([[subQ2,-1.0]])],"derivedFrom":subQ1}),1.0]])]});}
            var Q54;
            {var subQ0=sQuery(id+"F3.wireOp",EDGE,"E81.trimOffspring");var subQ1=sQuery(id+"F3.wireOp",EDGE,"E80.trimOffspring");var subQ2=makeQuery(id+"F3.imprint","INTERSECT",VERTEX,{"derivedFrom":[subQ1,subQ0]});Q54=makeQuery(id+"F3.imprint","IMPRINT",FACE,{"disambiguationData":[TD([[makeQuery(id+"F3.imprint","IMPRINT",EDGE,{"disambiguationData":[TD([[subQ2,-1.0]])],"derivedFrom":subQ1}),-1.0]])]});}
            var Q55;
            {var subQ0=sQuery(id+"F3.wireOp",EDGE,"E81.trimOffspring");var subQ1=sQuery(id+"F3.wireOp",EDGE,"E74.trimOffspring");var subQ2=makeQuery(id+"F3.imprint","INTERSECT",VERTEX,{"derivedFrom":[subQ1,subQ0]});Q55=makeQuery(id+"F3.imprint","IMPRINT",FACE,{"disambiguationData":[TD([[makeQuery(id+"F3.imprint","IMPRINT",EDGE,{"disambiguationData":[TD([[subQ2,-1.0]])],"derivedFrom":subQ1}),1.0]])]});}
            extrude(context, id + "F4", {"entities" : qUnion([Q0, Q1, Q2, Q3, Q4, Q5, Q6, Q7, Q8, Q9, Q10, Q11, Q12, Q13, Q14, Q15, Q16, Q17, Q18, Q19, Q20, Q21, Q22, Q23, Q24, Q25, Q26, Q27, Q28, Q29, Q30, Q31, Q32, Q33, Q34, Q35, Q36, Q37, Q38, Q39, Q40, Q41, Q42, Q43, Q44, Q45, Q46, Q47, Q48, Q49, Q50, Q51, Q52, Q53, Q54, Q55]), "operationType" : NewBodyOperationType.ADD, "depth" : 3 * mm, "offsetDistance" : 25 * mm});
        }
        {
            var Q0;
            Q0=sQuery(id+"F2.wireOp",VERTEX,"E11.center");
            var Q1;
            Q1=sQuery(id+"F2.wireOp",VERTEX,"E10.center");
            var Q2;
            Q2=makeQuery(id+"F1.opExtrude","SWEPT_BODY",BODY,{"disambiguationData":[OSD([sQuery(id+"F0.wireOp",EDGE,"E0"),sQuery(id+"F0.wireOp",EDGE,"E1"),sQuery(id+"F0.wireOp",EDGE,"E2"),sQuery(id+"F0.wireOp",EDGE,"E3"),sQuery(id+"F0.wireOp",EDGE,"E4"),sQuery(id+"F0.wireOp",EDGE,"E5"),sQuery(id+"F0.wireOp",EDGE,"E6"),sQuery(id+"F0.wireOp",EDGE,"E7"),sQuery(id+"F0.wireOp",EDGE,"E8"),sQuery(id+"F0.wireOp",EDGE,"E9.bottom"),sQuery(id+"F0.wireOp",EDGE,"E9.top"),sQuery(id+"F0.wireOp",EDGE,"E9.left"),sQuery(id+"F0.wireOp",EDGE,"E9.right")])]});
            hole(context, id + "F5", {"style" : HoleStyle.SIMPLE, "endStyle" : HoleEndStyle.THROUGH, "holeDiameter" : 6 * mm, "isTappedThrough" : true, "tappedDepth" : 12 * mm, "tapClearance" : 3, "locations" : qUnion([Q0, Q1]), "scope" : qUnion([Q2])});
        }
        {
            var Q0;
            Q0=makeQuery(id+"F4.opExtrude","SWEPT_EDGE",EDGE,{"disambiguationData":[OSD([sQuery(id+"F3.wireOp",EDGE,"E14"),sQuery(id+"F3.wireOp",EDGE,"E18")])]});
            var Q1;
            Q1=makeQuery(id+"F4.opExtrude","SWEPT_EDGE",EDGE,{"disambiguationData":[OSD([sQuery(id+"F3.wireOp",EDGE,"E17"),sQuery(id+"F3.wireOp",EDGE,"E45.trimOffspring")])]});
            var Q2;
            Q2=makeQuery(id+"F4.opExtrude","SWEPT_EDGE",EDGE,{"disambiguationData":[OSD([sQuery(id+"F3.wireOp",EDGE,"E19"),sQuery(id+"F3.wireOp",EDGE,"E47.trimOffspring")])]});
            var Q3;
            Q3=makeQuery(id+"F4.opExtrude","SWEPT_EDGE",EDGE,{"disambiguationData":[OSD([sQuery(id+"F3.wireOp",EDGE,"E22"),sQuery(id+"F3.wireOp",EDGE,"E47.trimOffspring")])]});
            var Q4;
            Q4=makeQuery(id+"F4.opExtrude","SWEPT_EDGE",EDGE,{"disambiguationData":[OSD([sQuery(id+"F3.wireOp",EDGE,"E50.trimOffspring"),sQuery(id+"F3.wireOp",EDGE,"E52")])]});
            var Q5;
            Q5=makeQuery(id+"F4.opExtrude","SWEPT_EDGE",EDGE,{"disambiguationData":[OSD([sQuery(id+"F3.wireOp",EDGE,"E16"),sQuery(id+"F3.wireOp",EDGE,"E50.trimOffspring")])]});
            var Q6;
            Q6=makeQuery(id+"F4.opExtrude","SWEPT_EDGE",EDGE,{"disambiguationData":[OSD([sQuery(id+"F3.wireOp",EDGE,"E15"),sQuery(id+"F3.wireOp",EDGE,"E63.trimOffspring")])]});
            var Q7;
            Q7=makeQuery(id+"F4.opExtrude","SWEPT_EDGE",EDGE,{"disambiguationData":[OSD([sQuery(id+"F3.wireOp",EDGE,"E23"),sQuery(id+"F3.wireOp",EDGE,"E63.trimOffspring")])]});
            var Q8;
            Q8=makeQuery(id+"F4.opExtrude","SWEPT_EDGE",EDGE,{"disambiguationData":[OSD([sQuery(id+"F3.wireOp",EDGE,"E57.trimOffspring"),sQuery(id+"F3.wireOp",EDGE,"E83")])]});
            var Q9;
            Q9=makeQuery(id+"F4.opExtrude","SWEPT_EDGE",EDGE,{"disambiguationData":[OSD([sQuery(id+"F3.wireOp",EDGE,"E26"),sQuery(id+"F3.wireOp",EDGE,"E57.trimOffspring")])]});
            var Q10;
            Q10=makeQuery(id+"F4.opExtrude","SWEPT_EDGE",EDGE,{"disambiguationData":[OSD([sQuery(id+"F3.wireOp",EDGE,"E25"),sQuery(id+"F3.wireOp",EDGE,"E60.trimOffspring")])]});
            var Q11;
            Q11=makeQuery(id+"F4.opExtrude","SWEPT_EDGE",EDGE,{"disambiguationData":[OSD([sQuery(id+"F3.wireOp",EDGE,"E60.trimOffspring"),sQuery(id+"F3.wireOp",EDGE,"E82")])]});
            var Q12;
            Q12=makeQuery(id+"F4.opExtrude","SWEPT_EDGE",EDGE,{"disambiguationData":[OSD([sQuery(id+"F3.wireOp",EDGE,"E28"),sQuery(id+"F3.wireOp",EDGE,"E69.trimOffspring")])]});
            var Q13;
            Q13=makeQuery(id+"F4.opExtrude","SWEPT_EDGE",EDGE,{"disambiguationData":[OSD([sQuery(id+"F3.wireOp",EDGE,"E31"),sQuery(id+"F3.wireOp",EDGE,"E69.trimOffspring")])]});
            var Q14;
            Q14=makeQuery(id+"F4.opExtrude","SWEPT_EDGE",EDGE,{"disambiguationData":[OSD([sQuery(id+"F3.wireOp",EDGE,"E30"),sQuery(id+"F3.wireOp",EDGE,"E75.trimOffspring")])]});
            var Q15;
            Q15=makeQuery(id+"F4.opExtrude","SWEPT_EDGE",EDGE,{"disambiguationData":[OSD([sQuery(id+"F3.wireOp",EDGE,"E33"),sQuery(id+"F3.wireOp",EDGE,"E75.trimOffspring")])]});
            var Q16;
            Q16=makeQuery(id+"F4.opExtrude","SWEPT_EDGE",EDGE,{"disambiguationData":[OSD([sQuery(id+"F3.wireOp",EDGE,"E32"),sQuery(id+"F3.wireOp",EDGE,"E77.trimOffspring")])]});
            var Q17;
            Q17=makeQuery(id+"F4.opExtrude","SWEPT_EDGE",EDGE,{"disambiguationData":[OSD([sQuery(id+"F3.wireOp",EDGE,"E78.trimOffspring"),sQuery(id+"F3.wireOp",EDGE,"E79.trimOffspring")])]});
            var Q18;
            Q18=makeQuery(id+"F4.opExtrude","SWEPT_EDGE",EDGE,{"disambiguationData":[OSD([sQuery(id+"F3.wireOp",EDGE,"E80.trimOffspring"),sQuery(id+"F3.wireOp",EDGE,"E81.trimOffspring")])]});
            var Q19;
            Q19=makeQuery(id+"F4.opExtrude","SWEPT_EDGE",EDGE,{"disambiguationData":[OSD([sQuery(id+"F3.wireOp",EDGE,"E74.trimOffspring"),sQuery(id+"F3.wireOp",EDGE,"E81.trimOffspring")])]});
            var Q20;
            Q20=makeQuery(id+"F4.opExtrude","SWEPT_EDGE",EDGE,{"disambiguationData":[OSD([sQuery(id+"F3.wireOp",EDGE,"E67.trimOffspring"),sQuery(id+"F3.wireOp",EDGE,"E73.trimOffspring")])]});
            var Q21;
            Q21=makeQuery(id+"F4.opExtrude","SWEPT_EDGE",EDGE,{"disambiguationData":[OSD([sQuery(id+"F3.wireOp",EDGE,"E67.trimOffspring"),sQuery(id+"F3.wireOp",EDGE,"E72.trimOffspring")])]});
            var Q22;
            Q22=makeQuery(id+"F4.opExtrude","SWEPT_EDGE",EDGE,{"disambiguationData":[OSD([sQuery(id+"F3.wireOp",EDGE,"E66.trimOffspring"),sQuery(id+"F3.wireOp",EDGE,"E70.trimOffspring")])]});
            var Q23;
            Q23=makeQuery(id+"F4.opExtrude","SWEPT_EDGE",EDGE,{"disambiguationData":[OSD([sQuery(id+"F3.wireOp",EDGE,"E61.trimOffspring"),sQuery(id+"F3.wireOp",EDGE,"E66.trimOffspring")])]});
            var Q24;
            Q24=makeQuery(id+"F4.opExtrude","SWEPT_EDGE",EDGE,{"disambiguationData":[OSD([sQuery(id+"F3.wireOp",EDGE,"E59.trimOffspring"),sQuery(id+"F3.wireOp",EDGE,"E65.trimOffspring")])]});
            var Q25;
            Q25=makeQuery(id+"F4.opExtrude","SWEPT_EDGE",EDGE,{"disambiguationData":[OSD([sQuery(id+"F3.wireOp",EDGE,"E58.trimOffspring"),sQuery(id+"F3.wireOp",EDGE,"E65.trimOffspring")])]});
            var Q26;
            Q26=makeQuery(id+"F4.opExtrude","SWEPT_EDGE",EDGE,{"disambiguationData":[OSD([sQuery(id+"F3.wireOp",EDGE,"E55.trimOffspring"),sQuery(id+"F3.wireOp",EDGE,"E56.trimOffspring")])]});
            var Q27;
            Q27=makeQuery(id+"F4.opExtrude","SWEPT_EDGE",EDGE,{"disambiguationData":[OSD([sQuery(id+"F3.wireOp",EDGE,"E54.trimOffspring"),sQuery(id+"F3.wireOp",EDGE,"E55.trimOffspring")])]});
            var Q28;
            Q28=makeQuery(id+"F4.opExtrude","SWEPT_EDGE",EDGE,{"disambiguationData":[OSD([sQuery(id+"F3.wireOp",EDGE,"E53.trimOffspring"),sQuery(id+"F3.wireOp",EDGE,"E64.trimOffspring")])]});
            var Q29;
            Q29=makeQuery(id+"F4.opExtrude","SWEPT_EDGE",EDGE,{"disambiguationData":[OSD([sQuery(id+"F3.wireOp",EDGE,"E51.trimOffspring"),sQuery(id+"F3.wireOp",EDGE,"E64.trimOffspring")])]});
            var Q30;
            Q30=makeQuery(id+"F4.opExtrude","SWEPT_EDGE",EDGE,{"disambiguationData":[OSD([sQuery(id+"F3.wireOp",EDGE,"E49.trimOffspring"),sQuery(id+"F3.wireOp",EDGE,"E62.trimOffspring")])]});
            var Q31;
            Q31=makeQuery(id+"F4.opExtrude","SWEPT_EDGE",EDGE,{"disambiguationData":[OSD([sQuery(id+"F3.wireOp",EDGE,"E48.trimOffspring"),sQuery(id+"F3.wireOp",EDGE,"E62.trimOffspring")])]});
            var Q32;
            Q32=makeQuery(id+"F4.opExtrude","SWEPT_EDGE",EDGE,{"disambiguationData":[OSD([sQuery(id+"F3.wireOp",EDGE,"E43.trimOffspring"),sQuery(id+"F3.wireOp",EDGE,"E44.trimOffspring")])]});
            var Q33;
            Q33=makeQuery(id+"F4.opExtrude","SWEPT_EDGE",EDGE,{"disambiguationData":[OSD([sQuery(id+"F3.wireOp",EDGE,"E43.trimOffspring"),sQuery(id+"F3.wireOp",EDGE,"E46.trimOffspring")])]});
            var Q34;
            Q34=makeQuery(id+"F4.opExtrude","SWEPT_EDGE",EDGE,{"disambiguationData":[OSD([sQuery(id+"F3.wireOp",EDGE,"E36"),sQuery(id+"F3.wireOp",EDGE,"E42.trimOffspring")])]});
            fillet(context, id + "F6", {"entities" : qUnion([Q0, Q1, Q2, Q3, Q4, Q5, Q6, Q7, Q8, Q9, Q10, Q11, Q12, Q13, Q14, Q15, Q16, Q17, Q18, Q19, Q20, Q21, Q22, Q23, Q24, Q25, Q26, Q27, Q28, Q29, Q30, Q31, Q32, Q33, Q34]), "radius" : 4 * mm, "tangentPropagation" : true, "allowEdgeOverflow" : false});
        }
        {
            var Q0;
            {var subQ0=sQuery(id+"F0.wireOp",EDGE,"E9.right");var subQ1=makeQuery(id+"F1.opExtrude","CAP_EDGE",EDGE,{"disambiguationData":[OSD([subQ0])],"isStart":false});Q0=makeQuery(id+"F4.opExtrude","CAP_EDGE",EDGE,{"disambiguationData":[OSD([subQ0]),TDD([makeQuery(id+"F3.imprint","IMPRINT",EDGE,{"disambiguationData":[TD([[makeQuery(id+"F3.imprint","INTERSECT",VERTEX,{"derivedFrom":[makeQuery(id+"F1.opExtrude","CAP_EDGE",EDGE,{"disambiguationData":[OSD([sQuery(id+"F0.wireOp",EDGE,"E9.bottom")])],"isStart":false}),subQ1]}),-1.0]])],"derivedFrom":subQ1})])],"isStart":false});}
            var Q1;
            {var subQ0=sQuery(id+"F0.wireOp",EDGE,"E9.right");var subQ1=makeQuery(id+"F1.opExtrude","CAP_EDGE",EDGE,{"disambiguationData":[OSD([subQ0])],"isStart":false});Q1=makeQuery(id+"F4.opExtrude","CAP_EDGE",EDGE,{"disambiguationData":[OSD([subQ0]),TDD([makeQuery(id+"F3.imprint","IMPRINT",EDGE,{"disambiguationData":[TD([[makeQuery(id+"F3.imprint","INTERSECT",VERTEX,{"derivedFrom":[makeQuery(id+"F1.opExtrude","CAP_EDGE",EDGE,{"disambiguationData":[OSD([sQuery(id+"F0.wireOp",EDGE,"E9.top")])],"isStart":false}),subQ1]}),1.0]])],"derivedFrom":subQ1})])],"isStart":false});}
            var Q2;
            Q2=makeQuery(id+"F4.opExtrude","CAP_EDGE",EDGE,{"disambiguationData":[OSD([sQuery(id+"F3.wireOp",EDGE,"E84")])],"isStart":false});
            var Q3;
            Q3=makeQuery(id+"F4.opExtrude","CAP_EDGE",EDGE,{"disambiguationData":[OSD([sQuery(id+"F3.wireOp",EDGE,"E34")])],"isStart":false});
            fillet(context, id + "F7", {"entities" : qUnion([Q0, Q1, Q2, Q3]), "radius" : 5 * mm, "tangentPropagation" : true, "allowEdgeOverflow" : false});
        }
        {
            var Q0;
            Q0=makeQuery(id+"F1.opExtrude","CAP_EDGE",EDGE,{"disambiguationData":[OSD([sQuery(id+"F0.wireOp",EDGE,"E8")])],"isStart":true});
            var Q1;
            Q1=makeQuery(id+"F1.opExtrude","CAP_EDGE",EDGE,{"disambiguationData":[OSD([sQuery(id+"F0.wireOp",EDGE,"E4")])],"isStart":true});
            var Q2;
            Q2=makeQuery(id+"F1.opExtrude","CAP_EDGE",EDGE,{"disambiguationData":[OSD([sQuery(id+"F0.wireOp",EDGE,"E5")])],"isStart":true});
            var Q3;
            Q3=makeQuery(id+"F1.opExtrude","CAP_FACE",FACE,{"disambiguationData":[OSD([sQuery(id+"F0.wireOp",EDGE,"E0"),sQuery(id+"F0.wireOp",EDGE,"E1"),sQuery(id+"F0.wireOp",EDGE,"E2"),sQuery(id+"F0.wireOp",EDGE,"E3"),sQuery(id+"F0.wireOp",EDGE,"E4"),sQuery(id+"F0.wireOp",EDGE,"E5"),sQuery(id+"F0.wireOp",EDGE,"E6"),sQuery(id+"F0.wireOp",EDGE,"E7"),sQuery(id+"F0.wireOp",EDGE,"E8"),sQuery(id+"F0.wireOp",EDGE,"E9.bottom"),sQuery(id+"F0.wireOp",EDGE,"E9.top"),sQuery(id+"F0.wireOp",EDGE,"E9.left"),sQuery(id+"F0.wireOp",EDGE,"E9.right")])],"isStart":true});
            fillet(context, id + "F8", {"entities" : qUnion([Q0, Q1, Q2, Q3]), "radius" : 1 * mm, "tangentPropagation" : true, "allowEdgeOverflow" : false});
        }
    });
